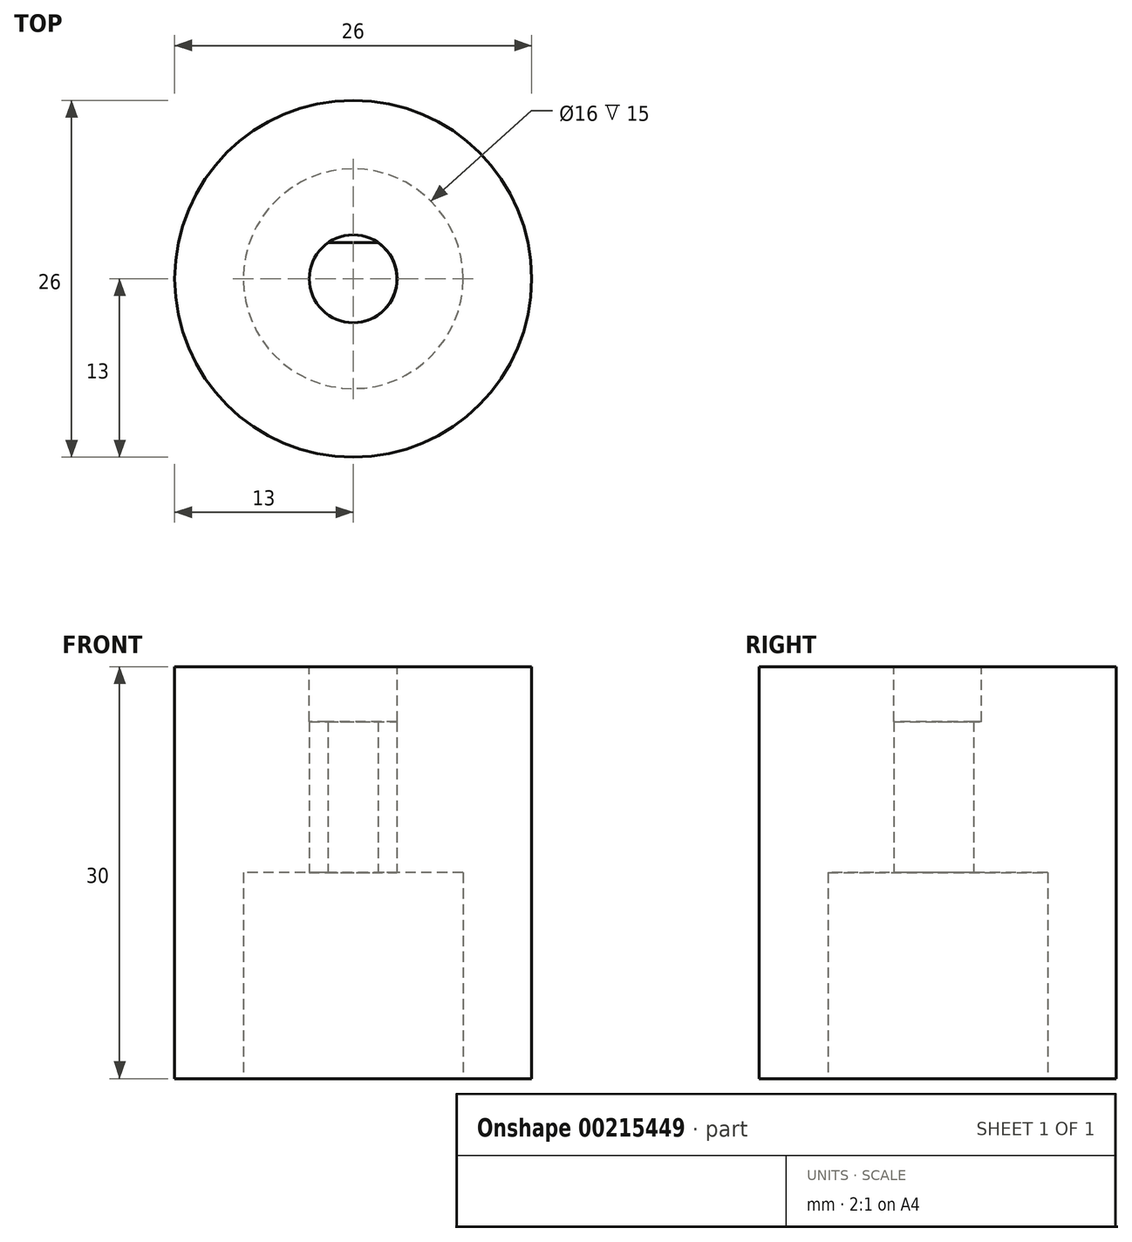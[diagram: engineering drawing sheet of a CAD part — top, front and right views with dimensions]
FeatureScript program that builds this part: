
annotation { "Feature Type Name" : "Feature", "Feature Type Description" : "" }
export const myFeature = defineFeature(function(context is Context, id is Id, definition is map)
    precondition{}
    {
        {
            var Q0;
            Q0=qCreatedBy(makeId("Top.planeOp"),FACE);
            var sketch = newSketch(context, id + "F0", { "sketchPlane" : qUnion([Q0])});
            skCircle(sketch, "E0", {"center": v(0, 0) * mm, "radius": 13 * mm});
            skSolve(sketch);
        }
        {
            var Q0;
            Q0=qCreatedBy(makeId("Top.planeOp"),FACE);
            cPlane(context, id + "F1", {"entities" : qUnion([Q0]), "cplaneType" : CPlaneType.OFFSET, "offset" : 15 * mm, "width" : 150 * mm, "height" : 150 * mm});
        }
        {
            var Q0;
            Q0=qCreatedBy(makeId("Top.planeOp"),FACE);
            cPlane(context, id + "F2", {"entities" : qUnion([Q0]), "cplaneType" : CPlaneType.OFFSET, "offset" : 15 * mm, "oppositeDirection" : true, "width" : 150 * mm, "height" : 150 * mm});
        }
        {
            var Q0;
            Q0=qCreatedBy(id+"F1.planeOp",FACE);
            var sketch = newSketch(context, id + "F3", { "sketchPlane" : qUnion([Q0])});
            skCircle(sketch, "E1", {"center": v(0, 0) * mm, "radius": 3.2 * mm});
            skSolve(sketch);
        }
        {
            var Q0;
            Q0=qCreatedBy(id+"F2.planeOp",FACE);
            var sketch = newSketch(context, id + "F4", { "sketchPlane" : qUnion([Q0])});
            skCircle(sketch, "E2", {"center": v(0, 0) * mm, "radius": 8 * mm});
            skSolve(sketch);
        }
        {
            var Q0;
            Q0 = qSketchRegion(id + "F0", true);
            extrude(context, id + "F5", {"entities" : qUnion([Q0]), "depth" : 30 * mm, "symmetric" : true});
        }
        {
            var Q0;
            Q0 = qSketchRegion(id + "F4", true);
            extrude(context, id + "F6", {"entities" : qUnion([Q0]), "operationType" : NewBodyOperationType.REMOVE, "depth" : 15 * mm});
        }
        {
            var Q0;
            Q0=qCreatedBy(makeId("Top.planeOp"),FACE);
            var sketch = newSketch(context, id + "F7", { "sketchPlane" : qUnion([Q0])});
            skLineSegment(sketch, "E3", {"start": v(-1.84, 2.62) * mm, "end": v(1.82, 2.62) * mm});
            skArc(sketch, "E4", {"start": v(-1.84, 2.62) * mm, "mid": v(-0.01, -3.2) * mm, "end": v(1.82, 2.62) * mm});
            skSolve(sketch);
        }
        {
            var Q0;
            Q0 = qSketchRegion(id + "F3", true);
            extrude(context, id + "F8", {"entities" : qUnion([Q0]), "operationType" : NewBodyOperationType.REMOVE, "oppositeDirection" : true, "depth" : 4 * mm});
        }
        {
            var Q0;
            Q0 = qSketchRegion(id + "F7", true);
            extrude(context, id + "F9", {"entities" : qUnion([Q0]), "operationType" : NewBodyOperationType.REMOVE, "depth" : 11 * mm});
        }
    });
